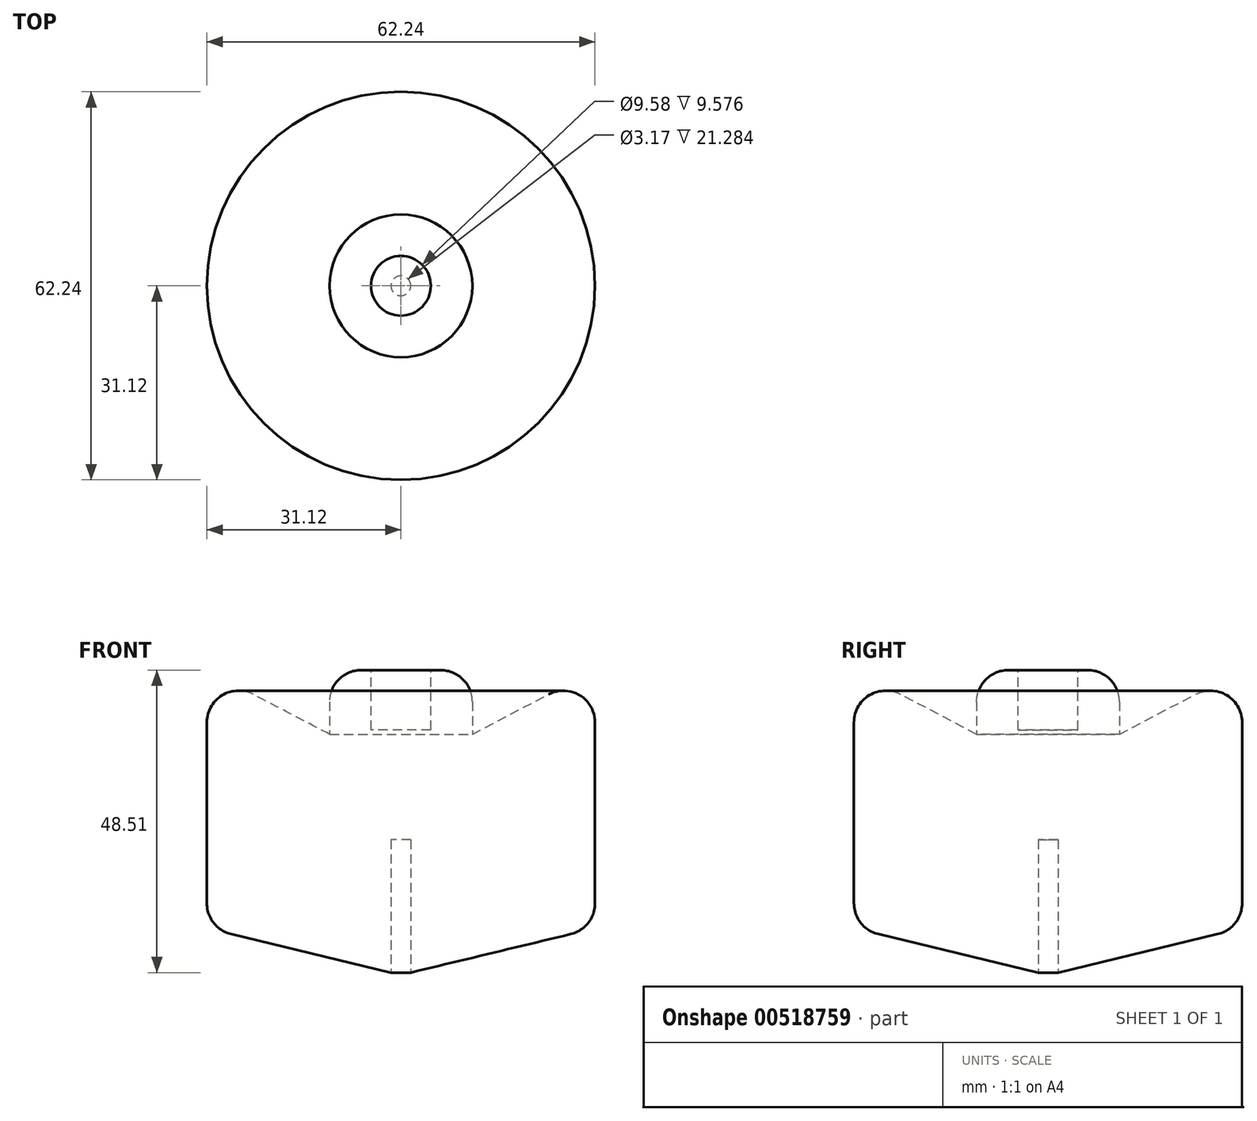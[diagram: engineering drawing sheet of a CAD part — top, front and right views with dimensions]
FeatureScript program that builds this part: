
annotation { "Feature Type Name" : "Feature", "Feature Type Description" : "" }
export const myFeature = defineFeature(function(context is Context, id is Id, definition is map)
    precondition{}
    {
        {
            var Q0;
            Q0=qCreatedBy(makeId("Front.planeOp"),FACE);
            var sketch = newSketch(context, id + "F0", { "sketchPlane" : qUnion([Q0])});
            skLineSegment(sketch, "E0", {"start": v(0, 0) * mm, "end": v(0, 48.89) * mm});
            skLineSegment(sketch, "E1", {"start": v(0, 48.89) * mm, "end": v(11.45, 48.89) * mm});
            skLineSegment(sketch, "E2", {"start": v(11.45, 48.89) * mm, "end": v(11.45, 38.61) * mm});
            skLineSegment(sketch, "E3", {"start": v(11.45, 38.61) * mm, "end": v(31.12, 48.89) * mm});
            skLineSegment(sketch, "E4", {"start": v(31.12, 48.89) * mm, "end": v(31.12, 7.49) * mm});
            skLineSegment(sketch, "E5", {"start": v(31.12, 7.49) * mm, "end": v(0, 0) * mm});
            skSolve(sketch);
        }
        {
            var Q0;
            Q0=makeQuery(id+"F0.imprint","IMPRINT",FACE,{"disambiguationData":[TD([[makeQuery(id+"F0.imprint","IMPRINT",EDGE,{"derivedFrom":sQuery(id+"F0.wireOp",EDGE,"E0")}),-1.0]])]});
            var Q1;
            Q1=sQuery(id+"F0.wireOp",EDGE,"E0");
            revolve(context, id + "F1", {"entities" : qUnion([Q0]), "axis" : qUnion([Q1]), "revolveType" : RevolveType.FULL});
        }
        {
            var Q0;
            Q0=makeQuery(id+"F1.opRevolve","SWEPT_FACE",FACE,{"disambiguationData":[OSD([sQuery(id+"F0.wireOp",EDGE,"E1")])]});
            var sketch = newSketch(context, id + "F2", { "sketchPlane" : qUnion([Q0])});
            skCircle(sketch, "E6", {"center": v(0, 0) * mm, "radius": 4.79 * mm});
            skSolve(sketch);
        }
        {
            var Q0;
            Q0=makeQuery(id+"F2.imprint","IMPRINT",FACE,{"disambiguationData":[TD([[makeQuery(id+"F2.imprint","IMPRINT",EDGE,{"derivedFrom":sQuery(id+"F2.wireOp",EDGE,"E6")}),1.0]])]});
            extrude(context, id + "F3", {"entities" : qUnion([Q0]), "operationType" : NewBodyOperationType.REMOVE, "oppositeDirection" : true, "depth" : 9.58 * mm, "offsetDistance" : 25.4 * mm});
        }
        {
            var Q0;
            Q0=makeQuery(id+"F1.opRevolve","SWEPT_FACE",FACE,{"disambiguationData":[OSD([sQuery(id+"F0.wireOp",EDGE,"E4")])]});
            var Q1;
            Q1=makeQuery(id+"F1.opRevolve","SWEPT_EDGE",EDGE,{"disambiguationData":[OSD([sQuery(id+"F0.wireOp",EDGE,"E1"),sQuery(id+"F0.wireOp",EDGE,"E2")])]});
            fillet(context, id + "F4", {"entities" : qUnion([Q0, Q1]), "radius" : 5.08 * mm, "tangentPropagation" : true, "allowEdgeOverflow" : false});
        }
        {
            var Q0;
            Q0=qCreatedBy(makeId("Top.planeOp"),FACE);
            var sketch = newSketch(context, id + "F5", { "sketchPlane" : qUnion([Q0])});
            skCircle(sketch, "E7", {"center": v(0, 0) * mm, "radius": 1.59 * mm});
            skSolve(sketch);
        }
        {
            var Q0;
            Q0 = qSketchRegion(id + "F5", true);
            extrude(context, id + "F6", {"entities" : qUnion([Q0]), "operationType" : NewBodyOperationType.REMOVE, "depth" : 21.67 * mm, "offsetDistance" : 25.4 * mm});
        }
    });
